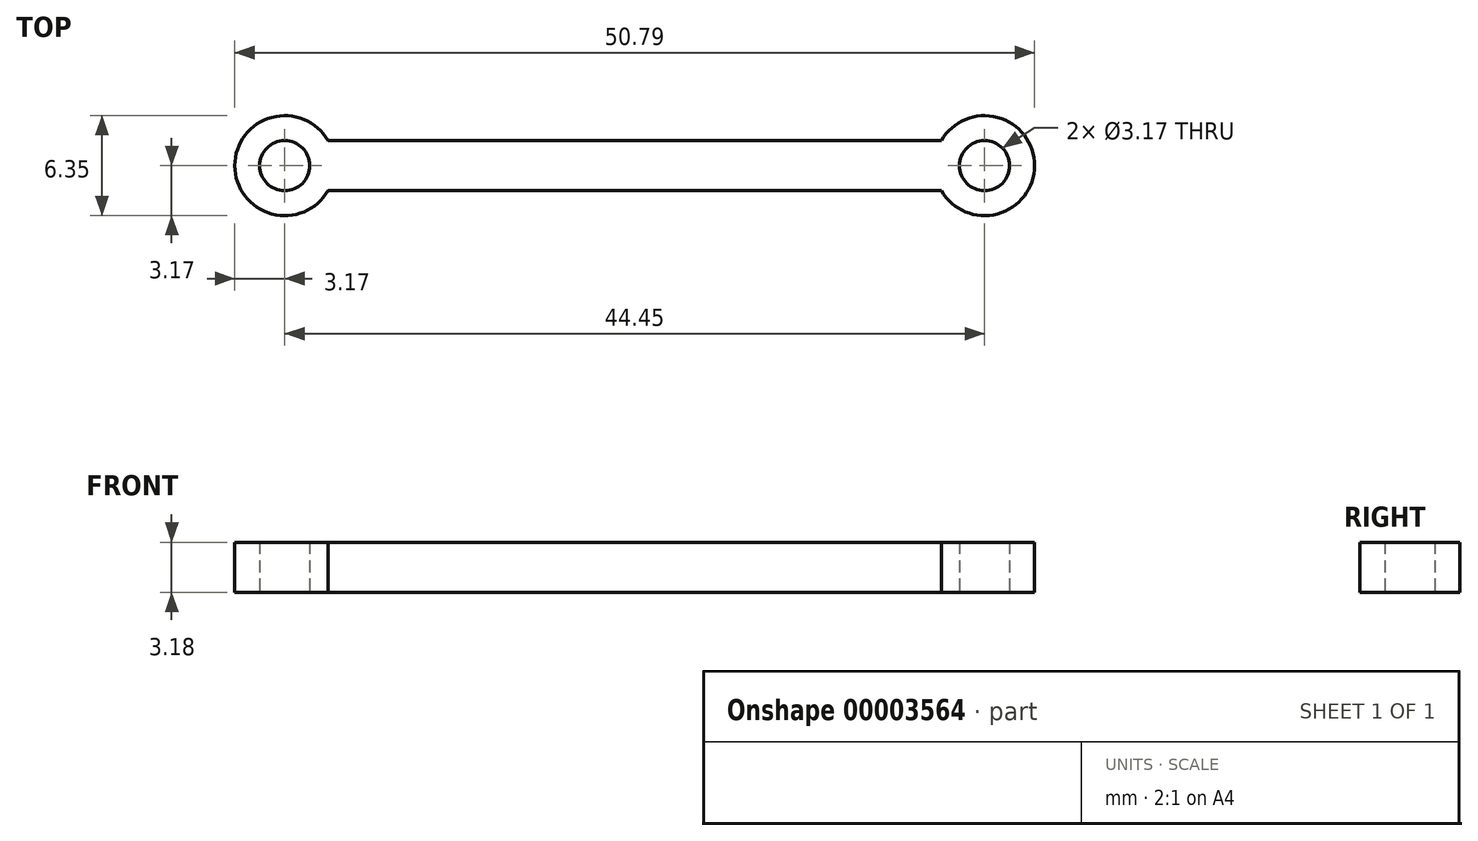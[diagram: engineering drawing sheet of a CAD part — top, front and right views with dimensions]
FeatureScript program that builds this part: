
annotation { "Feature Type Name" : "Feature", "Feature Type Description" : "" }
export const myFeature = defineFeature(function(context is Context, id is Id, definition is map)
    precondition{}
    {
        {
            var Q0;
            Q0=qCreatedBy(makeId("Top.planeOp"),FACE);
            var sketch = newSketch(context, id + "F0", { "sketchPlane" : qUnion([Q0])});
            skCircle(sketch, "E0", {"center": v(0, 0) * mm, "radius": 1.59 * mm});
            skArc(sketch, "E1", {"start": v(2.75, 1.59) * mm, "mid": v(-3.18, 0) * mm, "end": v(2.75, -1.59) * mm});
            skLineSegment(sketch, "E2", {"start": v(0, 0) * mm, "end": v(44.45, 0) * mm, "construction": true});
            skCircle(sketch, "E3", {"center": v(44.45, 0) * mm, "radius": 1.59 * mm});
            skArc(sketch, "E4", {"start": v(41.7, -1.59) * mm, "mid": v(47.62, 0) * mm, "end": v(41.7, 1.59) * mm});
            skLineSegment(sketch, "E5", {"start": v(2.75, 1.59) * mm, "end": v(41.7, 1.59) * mm});
            skLineSegment(sketch, "E6", {"start": v(2.75, -1.59) * mm, "end": v(41.7, -1.59) * mm});
            skSolve(sketch);
        }
        {
            var Q0;
            Q0 = qSketchRegion(id + "F0", true);
            extrude(context, id + "F1", {"entities" : qUnion([Q0]), "depth" : 3.17 * mm});
        }
    });
